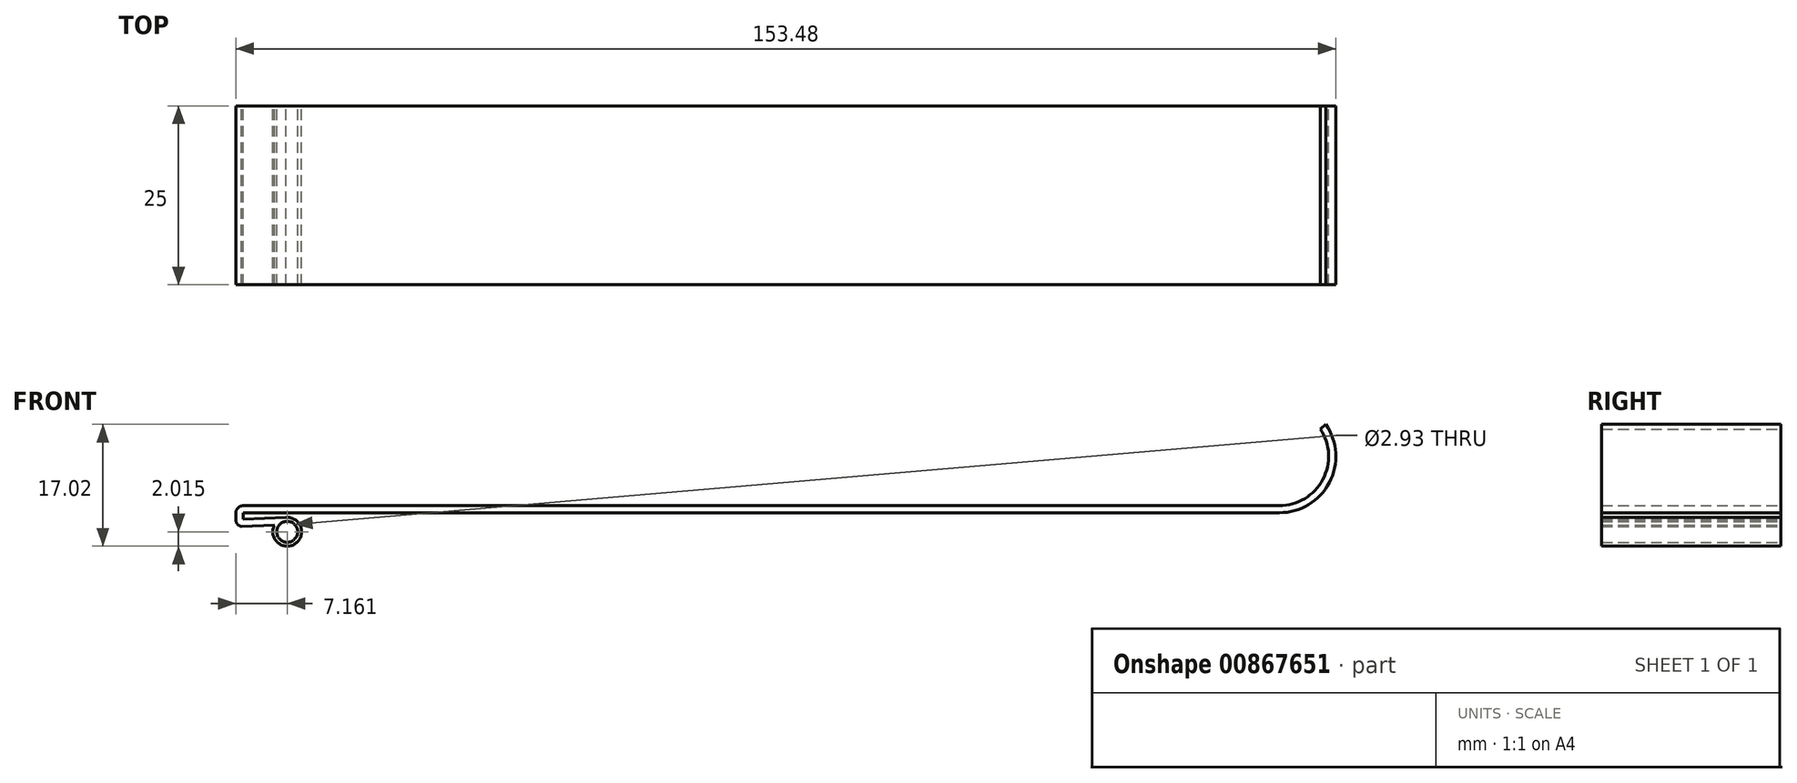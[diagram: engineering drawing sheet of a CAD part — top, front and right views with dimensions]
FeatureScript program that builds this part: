
annotation { "Feature Type Name" : "Feature", "Feature Type Description" : "" }
export const myFeature = defineFeature(function(context is Context, id is Id, definition is map)
    precondition{}
    {
        {
            var Q0;
            Q0=qCreatedBy(makeId("Front.planeOp"),FACE);
            var sketch = newSketch(context, id + "F0", { "sketchPlane" : qUnion([Q0])});
            skLineSegment(sketch, "E0", {"start": v(-87.65, 29.96) * mm, "end": v(56.82, 29.96) * mm});
            skArc(sketch, "E1", {"start": v(56.82, 29.96) * mm, "mid": v(62.89, 33.6) * mm, "end": v(62.55, 40.65) * mm});
            skArc(sketch, "E2.0", {"start": v(56.82, 28.96) * mm, "mid": v(63.8, 33.17) * mm, "end": v(63.31, 41.3) * mm});
            skLineSegment(sketch, "E2.1", {"start": v(-87.78, 28.96) * mm, "end": v(56.82, 28.96) * mm});
            skLineSegment(sketch, "E3", {"start": v(-87.78, 28.96) * mm, "end": v(-87.78, 28.07) * mm});
            skLineSegment(sketch, "E4", {"start": v(-87.78, 28.07) * mm, "end": v(-81.67, 28.32) * mm});
            skLineSegment(sketch, "E5.0", {"start": v(-87.99, 27.06) * mm, "end": v(-83.4, 27.24) * mm});
            skLineSegment(sketch, "E6.0", {"start": v(-88.78, 29.05) * mm, "end": v(-88.78, 27.95) * mm});
            skFitSpline(sketch, "E7", {"points": [v(-88.78, 27.95) * mm, v(-87.99, 27.06) * mm], "startDerivative": vector(0.02, -1.3) * mm, "endDerivative": vector(1.63, -0.25) * mm});
            skFitSpline(sketch, "E8", {"points": [v(-87.65, 29.96) * mm, v(-88.78, 29.05) * mm], "startDerivative": vector(-1.95, 0) * mm, "endDerivative": vector(-0.08, -1.37) * mm});
            skArc(sketch, "E9", {"start": v(-81.4, 28.3) * mm, "mid": v(-81.6, 28.33) * mm, "end": v(-81.8, 28.3) * mm});
            skArc(sketch, "E10", {"start": v(-83.4, 27.24) * mm, "mid": v(-80.5, 24.63) * mm, "end": v(-81.8, 28.3) * mm});
            skCircle(sketch, "E11", {"center": v(-81.62, 26.3) * mm, "radius": 1.46 * mm});
            skLineSegment(sketch, "E12", {"start": v(62.55, 40.65) * mm, "end": v(63.31, 41.3) * mm});
            skSolve(sketch);
        }
        {
            var Q0;
            Q0=makeQuery(id+"F0.imprint","IMPRINT",FACE,{"disambiguationData":[TD([[makeQuery(id+"F0.imprint","IMPRINT",EDGE,{"derivedFrom":sQuery(id+"F0.wireOp",EDGE,"E0")}),-1.0]])]});
            extrude(context, id + "F1", {"entities" : qUnion([Q0]), "depth" : 25 * mm, "offsetDistance" : 25 * mm});
        }
    });
